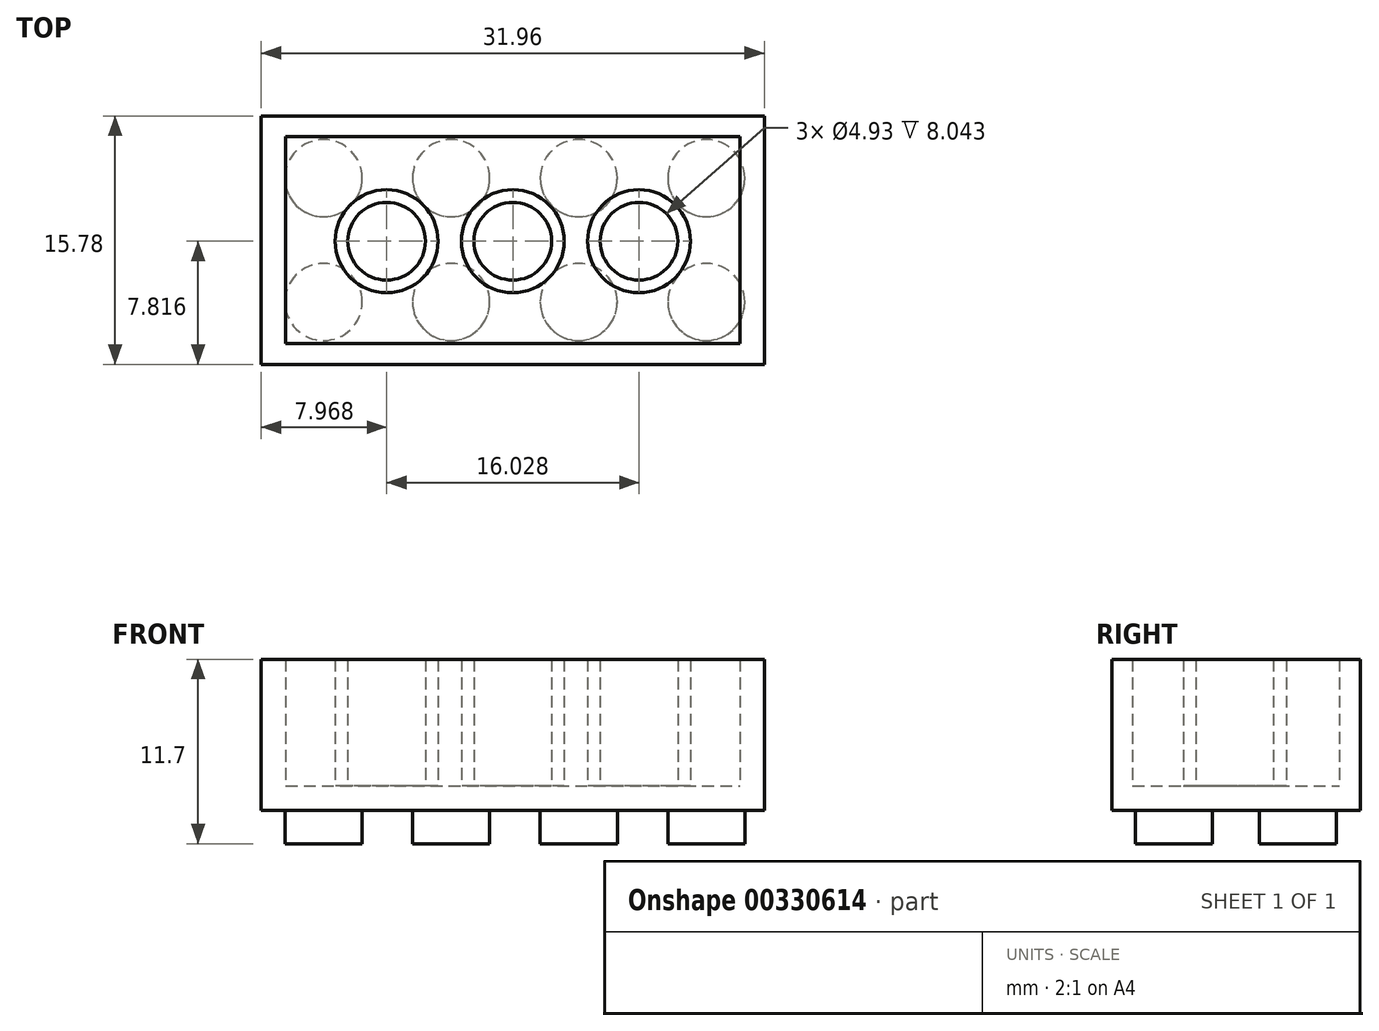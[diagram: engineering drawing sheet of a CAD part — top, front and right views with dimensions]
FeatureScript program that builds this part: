
annotation { "Feature Type Name" : "Feature", "Feature Type Description" : "" }
export const myFeature = defineFeature(function(context is Context, id is Id, definition is map)
    precondition{}
    {
        {
            var Q0;
            Q0=qCreatedBy(makeId("Top.planeOp"),FACE);
            var sketch = newSketch(context, id + "F0", { "sketchPlane" : qUnion([Q0])});
            skLineSegment(sketch, "E0.bottom", {"start": v(-36.9, -20.53) * mm, "end": v(-4.95, -20.53) * mm});
            skLineSegment(sketch, "E0.top", {"start": v(-36.9, -4.75) * mm, "end": v(-4.95, -4.75) * mm});
            skLineSegment(sketch, "E0.left", {"start": v(-36.9, -20.53) * mm, "end": v(-36.9, -4.75) * mm});
            skLineSegment(sketch, "E0.right", {"start": v(-4.95, -20.53) * mm, "end": v(-4.95, -4.75) * mm});
            skLineSegment(sketch, "E1.bottom", {"start": v(-35.35, -19.2) * mm, "end": v(-6.5, -19.2) * mm});
            skLineSegment(sketch, "E1.top", {"start": v(-35.35, -6.08) * mm, "end": v(-6.5, -6.08) * mm});
            skLineSegment(sketch, "E1.left", {"start": v(-35.35, -19.2) * mm, "end": v(-35.35, -6.08) * mm});
            skLineSegment(sketch, "E1.right", {"start": v(-6.5, -19.2) * mm, "end": v(-6.5, -6.08) * mm});
            skSolve(sketch);
        }
        {
            var Q0;
            Q0=qSketchRegion(id+"F0",true);
            var Q1;
            Q1=makeQuery(id+"F0.imprint","IMPRINT",FACE,{"disambiguationData":[TD([[makeQuery(id+"F0.imprint","IMPRINT",EDGE,{"derivedFrom":sQuery(id+"F0.wireOp",EDGE,"E1.bottom")}),1.0]])]});
            extrude(context, id + "F1", {"entities" : qUnion([Q0, Q1]), "depth" : 9.6 * mm});
        }
        {
            var Q0;
            Q0=makeQuery(id+"F0.imprint","IMPRINT",FACE,{"disambiguationData":[TD([[makeQuery(id+"F0.imprint","IMPRINT",EDGE,{"derivedFrom":sQuery(id+"F0.wireOp",EDGE,"E1.bottom")}),1.0]])]});
            extrude(context, id + "F2", {"entities" : qUnion([Q0]), "operationType" : NewBodyOperationType.REMOVE, "depth" : 25 * mm});
        }
        {
            var Q0;
            Q0=makeQuery(id+"F0.imprint","IMPRINT",FACE,{"disambiguationData":[TD([[makeQuery(id+"F0.imprint","IMPRINT",EDGE,{"derivedFrom":sQuery(id+"F0.wireOp",EDGE,"E1.bottom")}),1.0]])]});
            extrude(context, id + "F3", {"entities" : qUnion([Q0]), "operationType" : NewBodyOperationType.ADD, "depth" : 1.56 * mm});
        }
        {
            var Q0;
            Q0=makeQuery(id+"F3.opExtrude","CAP_FACE",FACE,{"disambiguationData":[OSD([sQuery(id+"F0.wireOp",EDGE,"E1.bottom"),sQuery(id+"F0.wireOp",EDGE,"E1.top"),sQuery(id+"F0.wireOp",EDGE,"E1.left"),sQuery(id+"F0.wireOp",EDGE,"E1.right")])],"isStart":false});
            var sketch = newSketch(context, id + "F4", { "sketchPlane" : qUnion([Q0])});
            skCircle(sketch, "E2", {"center": v(-28.94, -12.71) * mm, "radius": 2.47 * mm});
            skCircle(sketch, "E3", {"center": v(-28.94, -12.71) * mm, "radius": 3.27 * mm});
            skCircle(sketch, "E4", {"center": v(-20.93, -12.71) * mm, "radius": 2.47 * mm});
            skCircle(sketch, "E5", {"center": v(-20.93, -12.71) * mm, "radius": 3.27 * mm});
            skCircle(sketch, "E6", {"center": v(-12.91, -12.71) * mm, "radius": 2.47 * mm});
            skCircle(sketch, "E7", {"center": v(-12.91, -12.71) * mm, "radius": 3.27 * mm});
            skSolve(sketch);
        }
        {
            var Q0;
            Q0=makeQuery(id+"F4.imprint","IMPRINT",FACE,{"disambiguationData":[TD([[makeQuery(id+"F4.imprint","IMPRINT",EDGE,{"derivedFrom":sQuery(id+"F4.wireOp",EDGE,"E2")}),-1.0]])]});
            var Q1;
            Q1=makeQuery(id+"F4.imprint","IMPRINT",FACE,{"disambiguationData":[TD([[makeQuery(id+"F4.imprint","IMPRINT",EDGE,{"derivedFrom":sQuery(id+"F4.wireOp",EDGE,"E4")}),-1.0]])]});
            var Q2;
            Q2=makeQuery(id+"F4.imprint","IMPRINT",FACE,{"disambiguationData":[TD([[makeQuery(id+"F4.imprint","IMPRINT",EDGE,{"derivedFrom":sQuery(id+"F4.wireOp",EDGE,"E6")}),-1.0]])]});
            extrude(context, id + "F5", {"entities" : qUnion([Q0, Q1, Q2]), "operationType" : NewBodyOperationType.ADD, "depth" : 8.04 * mm});
        }
        {
            var Q0;
            Q0=makeQuery(id+"F3.boolean.opBoolean","MERGE",FACE,{"derivedFrom":[makeQuery(id+"F1.opExtrude","CAP_FACE",FACE,{"disambiguationData":[OSD([sQuery(id+"F0.wireOp",EDGE,"E0.bottom"),sQuery(id+"F0.wireOp",EDGE,"E0.top"),sQuery(id+"F0.wireOp",EDGE,"E0.left"),sQuery(id+"F0.wireOp",EDGE,"E0.right")])],"isStart":true}),makeQuery(id+"F3.opExtrude","CAP_FACE",FACE,{"disambiguationData":[OSD([sQuery(id+"F0.wireOp",EDGE,"E1.bottom"),sQuery(id+"F0.wireOp",EDGE,"E1.top"),sQuery(id+"F0.wireOp",EDGE,"E1.left"),sQuery(id+"F0.wireOp",EDGE,"E1.right")])],"isStart":true})]});
            var sketch = newSketch(context, id + "F6", { "sketchPlane" : qUnion([Q0])});
            skCircle(sketch, "E8", {"center": v(-32.95, 16.57) * mm, "radius": 2.45 * mm});
            skCircle(sketch, "E9", {"center": v(-24.84, 16.57) * mm, "radius": 2.45 * mm});
            skCircle(sketch, "E10", {"center": v(-16.74, 16.57) * mm, "radius": 2.45 * mm});
            skCircle(sketch, "E11", {"center": v(-8.64, 16.57) * mm, "radius": 2.45 * mm});
            skCircle(sketch, "E12", {"center": v(-32.95, 8.7) * mm, "radius": 2.45 * mm});
            skCircle(sketch, "E13", {"center": v(-24.84, 8.7) * mm, "radius": 2.45 * mm});
            skCircle(sketch, "E14", {"center": v(-16.74, 8.7) * mm, "radius": 2.45 * mm});
            skCircle(sketch, "E15", {"center": v(-8.64, 8.7) * mm, "radius": 2.45 * mm});
            skSolve(sketch);
        }
        {
            var Q0;
            Q0=makeQuery(id+"F6.imprint","IMPRINT",FACE,{"disambiguationData":[TD([[makeQuery(id+"F6.imprint","IMPRINT",EDGE,{"derivedFrom":sQuery(id+"F6.wireOp",EDGE,"E8")}),1.0]])]});
            var Q1;
            Q1=makeQuery(id+"F6.imprint","IMPRINT",FACE,{"disambiguationData":[TD([[makeQuery(id+"F6.imprint","IMPRINT",EDGE,{"derivedFrom":sQuery(id+"F6.wireOp",EDGE,"E9")}),1.0]])]});
            var Q2;
            Q2=makeQuery(id+"F6.imprint","IMPRINT",FACE,{"disambiguationData":[TD([[makeQuery(id+"F6.imprint","IMPRINT",EDGE,{"derivedFrom":sQuery(id+"F6.wireOp",EDGE,"E10")}),1.0]])]});
            var Q3;
            Q3=makeQuery(id+"F6.imprint","IMPRINT",FACE,{"disambiguationData":[TD([[makeQuery(id+"F6.imprint","IMPRINT",EDGE,{"derivedFrom":sQuery(id+"F6.wireOp",EDGE,"E11")}),1.0]])]});
            var Q4;
            Q4=makeQuery(id+"F6.imprint","IMPRINT",FACE,{"disambiguationData":[TD([[makeQuery(id+"F6.imprint","IMPRINT",EDGE,{"derivedFrom":sQuery(id+"F6.wireOp",EDGE,"E15")}),1.0]])]});
            var Q5;
            Q5=makeQuery(id+"F6.imprint","IMPRINT",FACE,{"disambiguationData":[TD([[makeQuery(id+"F6.imprint","IMPRINT",EDGE,{"derivedFrom":sQuery(id+"F6.wireOp",EDGE,"E14")}),1.0]])]});
            var Q6;
            Q6=makeQuery(id+"F6.imprint","IMPRINT",FACE,{"disambiguationData":[TD([[makeQuery(id+"F6.imprint","IMPRINT",EDGE,{"derivedFrom":sQuery(id+"F6.wireOp",EDGE,"E13")}),1.0]])]});
            var Q7;
            Q7=makeQuery(id+"F6.imprint","IMPRINT",FACE,{"disambiguationData":[TD([[makeQuery(id+"F6.imprint","IMPRINT",EDGE,{"derivedFrom":sQuery(id+"F6.wireOp",EDGE,"E12")}),1.0]])]});
            extrude(context, id + "F7", {"entities" : qUnion([Q0, Q1, Q2, Q3, Q4, Q5, Q6, Q7]), "operationType" : NewBodyOperationType.ADD, "depth" : 2.1 * mm});
        }
    });
